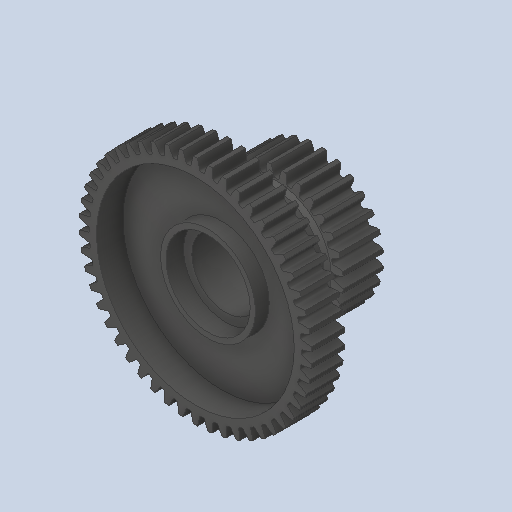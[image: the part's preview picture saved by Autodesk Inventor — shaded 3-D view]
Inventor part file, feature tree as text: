
AUTODESK INVENTOR PART (.ipt)
format: ipt  version: 2023 (Build 270158000, 158)  size: 717,824 bytes
history: native  units: in
note: dims shown in document units (in); Inventor stores cm internally (conversion verified against a paired STEP export)
features: chamfer x1
ambient origin geometry x8: Origin, YZ Plane, XZ Plane, XY Plane, X Axis, Y Axis, Z Axis, Center Point
bodies: Solid1 (feature_tree)
feature tree (1):
  chamfer  "Chamfer1"  [1 undecoded]
note: 1 required parameter value undecoded (feature->parameter linkage not recoverable at this tier; creation-order binding heuristic only, values carry confidence <= 0.55)
